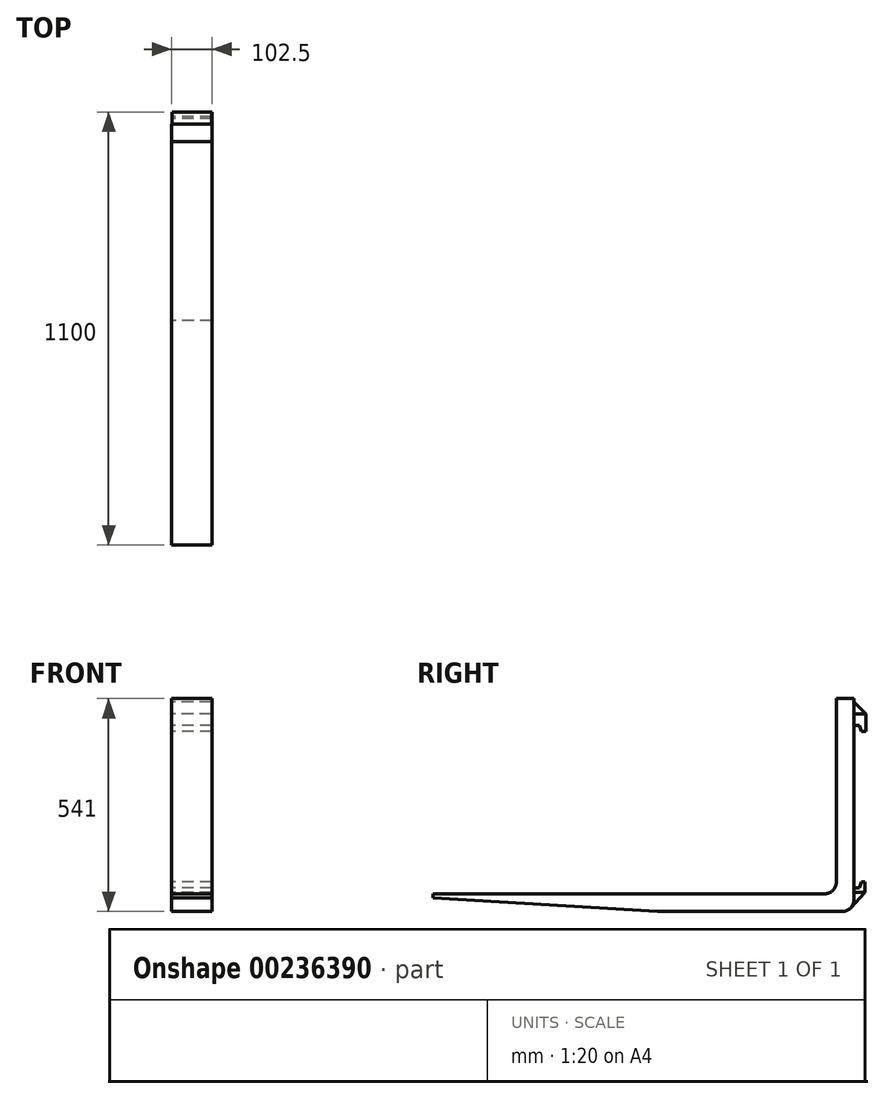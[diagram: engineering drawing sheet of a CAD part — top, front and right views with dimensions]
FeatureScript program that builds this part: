
annotation { "Feature Type Name" : "Feature", "Feature Type Description" : "" }
export const myFeature = defineFeature(function(context is Context, id is Id, definition is map)
    precondition{}
    {
        {
            var Q0;
            Q0=qCreatedBy(makeId("Right.planeOp"),FACE);
            var sketch = newSketch(context, id + "F0", { "sketchPlane" : qUnion([Q0])});
            skLineSegment(sketch, "E0", {"start": v(-455, -45) * mm, "end": v(45, -45) * mm});
            skLineSegment(sketch, "E1", {"start": v(45, -45) * mm, "end": v(45, 496) * mm});
            skLineSegment(sketch, "E2", {"start": v(45, 496) * mm, "end": v(0, 496) * mm});
            skLineSegment(sketch, "E3", {"start": v(0, 496) * mm, "end": v(0, 0) * mm});
            skLineSegment(sketch, "E4", {"start": v(0, 0) * mm, "end": v(-1025, 0) * mm});
            skLineSegment(sketch, "E5", {"start": v(-1025, 0) * mm, "end": v(-1025, -10) * mm});
            skLineSegment(sketch, "E6", {"start": v(-1025, -10) * mm, "end": v(-455, -45) * mm});
            skSolve(sketch);
        }
        {
            var Q0;
            Q0 = qSketchRegion(id + "F0", true);
            extrude(context, id + "F1", {"entities" : qUnion([Q0]), "endBound" : BoundingType.SYMMETRIC, "depth" : 102.5 * mm});
        }
        {
            var Q0;
            Q0=makeQuery(id+"F1.opExtrude","SWEPT_EDGE",EDGE,{"disambiguationData":[OSD([sQuery(id+"F0.wireOp",EDGE,"E3"),sQuery(id+"F0.wireOp",EDGE,"E4")])]});
            var Q1;
            Q1=makeQuery(id+"F1.opExtrude","SWEPT_EDGE",EDGE,{"disambiguationData":[OSD([sQuery(id+"F0.wireOp",EDGE,"E0"),sQuery(id+"F0.wireOp",EDGE,"E1")])]});
            fillet(context, id + "F2", {"entities" : qUnion([Q0, Q1]), "radius" : 30 * mm, "tangentPropagation" : true, "allowEdgeOverflow" : false});
        }
        {
            var Q0;
            Q0=qCreatedBy(makeId("Right.planeOp"),FACE);
            var sketch = newSketch(context, id + "F3", { "sketchPlane" : qUnion([Q0])});
            skLineSegment(sketch, "E7", {"start": v(45, 3) * mm, "end": v(45, 15) * mm});
            skLineSegment(sketch, "E8", {"start": v(45, 15) * mm, "end": v(59, 15) * mm});
            skLineSegment(sketch, "E9", {"start": v(59, 15) * mm, "end": v(64, 30) * mm});
            skLineSegment(sketch, "E10", {"start": v(64, 30) * mm, "end": v(72.5, 30) * mm});
            skLineSegment(sketch, "E11", {"start": v(72.5, 30) * mm, "end": v(72.5, 3) * mm});
            skLineSegment(sketch, "E12", {"start": v(72.5, 3) * mm, "end": v(45, 3) * mm});
            skSolve(sketch);
        }
        {
            var Q0;
            Q0=makeQuery(id+"F3.imprint","IMPRINT",FACE,{"disambiguationData":[TD([[makeQuery(id+"F3.imprint","IMPRINT",EDGE,{"derivedFrom":sQuery(id+"F3.wireOp",EDGE,"E7")}),-1.0]])]});
            var Q1;
            Q1 = qBodyType(qCreatedBy(id + "F3" ,EDGE), BodyType.WIRE);
            extrude(context, id + "F9", {"entities" : qUnion([Q0]), "operationType" : NewBodyOperationType.ADD, "surfaceEntities" : qUnion([Q1]), "endBound" : BoundingType.SYMMETRIC, "depth" : 101.6 * mm});
        }
        {
            var Q0;
            Q0=qCreatedBy(makeId("Right.planeOp"),FACE);
            var sketch = newSketch(context, id + "F4", { "sketchPlane" : qUnion([Q0])});
            skLineSegment(sketch, "E13", {"start": v(45, 457.5) * mm, "end": v(75, 457.5) * mm});
            skLineSegment(sketch, "E14", {"start": v(75, 457.5) * mm, "end": v(75, 413) * mm});
            skLineSegment(sketch, "E15", {"start": v(75, 413) * mm, "end": v(63.7, 413) * mm});
            skLineSegment(sketch, "E16", {"start": v(63.7, 413) * mm, "end": v(58, 428) * mm});
            skLineSegment(sketch, "E17", {"start": v(58, 428) * mm, "end": v(45, 428) * mm});
            skLineSegment(sketch, "E18", {"start": v(45, 428) * mm, "end": v(45, 457.5) * mm});
            skSolve(sketch);
        }
        {
            var Q0;
            Q0=makeQuery(id+"F4.imprint","IMPRINT",FACE,{"disambiguationData":[TD([[makeQuery(id+"F4.imprint","IMPRINT",EDGE,{"derivedFrom":sQuery(id+"F4.wireOp",EDGE,"E13")}),-1.0]])]});
            extrude(context, id + "F5", {"entities" : qUnion([Q0]), "operationType" : NewBodyOperationType.ADD, "endBound" : BoundingType.SYMMETRIC, "depth" : 101.6 * mm});
        }
        {
            var Q0;
            Q0=qCreatedBy(makeId("Right.planeOp"),FACE);
            var sketch = newSketch(context, id + "F6", { "sketchPlane" : qUnion([Q0])});
            skLineSegment(sketch, "E19", {"start": v(45, 3) * mm, "end": v(45, -15) * mm});
            skLineSegment(sketch, "E20", {"start": v(45, 3) * mm, "end": v(72.5, 3) * mm});
            skLineSegment(sketch, "E21", {"start": v(72.5, 3) * mm, "end": v(37.03, -35.37) * mm});
            skArc(sketch, "E22", {"start": v(45, -15) * mm, "mid": v(42.94, -25.94) * mm, "end": v(37.03, -35.37) * mm});
            skLineSegment(sketch, "E23", {"start": v(45, 487.5) * mm, "end": v(45, 457.5) * mm});
            skLineSegment(sketch, "E24", {"start": v(45, 457.5) * mm, "end": v(75, 457.5) * mm});
            skLineSegment(sketch, "E25", {"start": v(75, 457.5) * mm, "end": v(45, 487.5) * mm});
            skSolve(sketch);
        }
        {
            var Q0;
            Q0 = qSketchRegion(id + "F6", true);
            extrude(context, id + "F7", {"entities" : qUnion([Q0]), "operationType" : NewBodyOperationType.ADD, "endBound" : BoundingType.SYMMETRIC, "depth" : 100 * mm});
        }
        {
            var Q0;
            Q0=makeQuery(id+"F1.opExtrude","CAP_FACE",FACE,{"disambiguationData":[OSD([sQuery(id+"F0.wireOp",EDGE,"E0"),sQuery(id+"F0.wireOp",EDGE,"E1"),sQuery(id+"F0.wireOp",EDGE,"E2"),sQuery(id+"F0.wireOp",EDGE,"E3"),sQuery(id+"F0.wireOp",EDGE,"E4"),sQuery(id+"F0.wireOp",EDGE,"E5"),sQuery(id+"F0.wireOp",EDGE,"E6")])],"isStart":true});
            var sketch = newSketch(context, id + "F8", { "sketchPlane" : qUnion([Q0])});
            skCircle(sketch, "E26", {"center": v(-53.1, 418.1) * mm, "radius": 8.1 * mm});
            skCircle(sketch, "E27", {"center": v(-53.1, 23.1) * mm, "radius": 8.1 * mm});
            skSolve(sketch);
        }
    });
